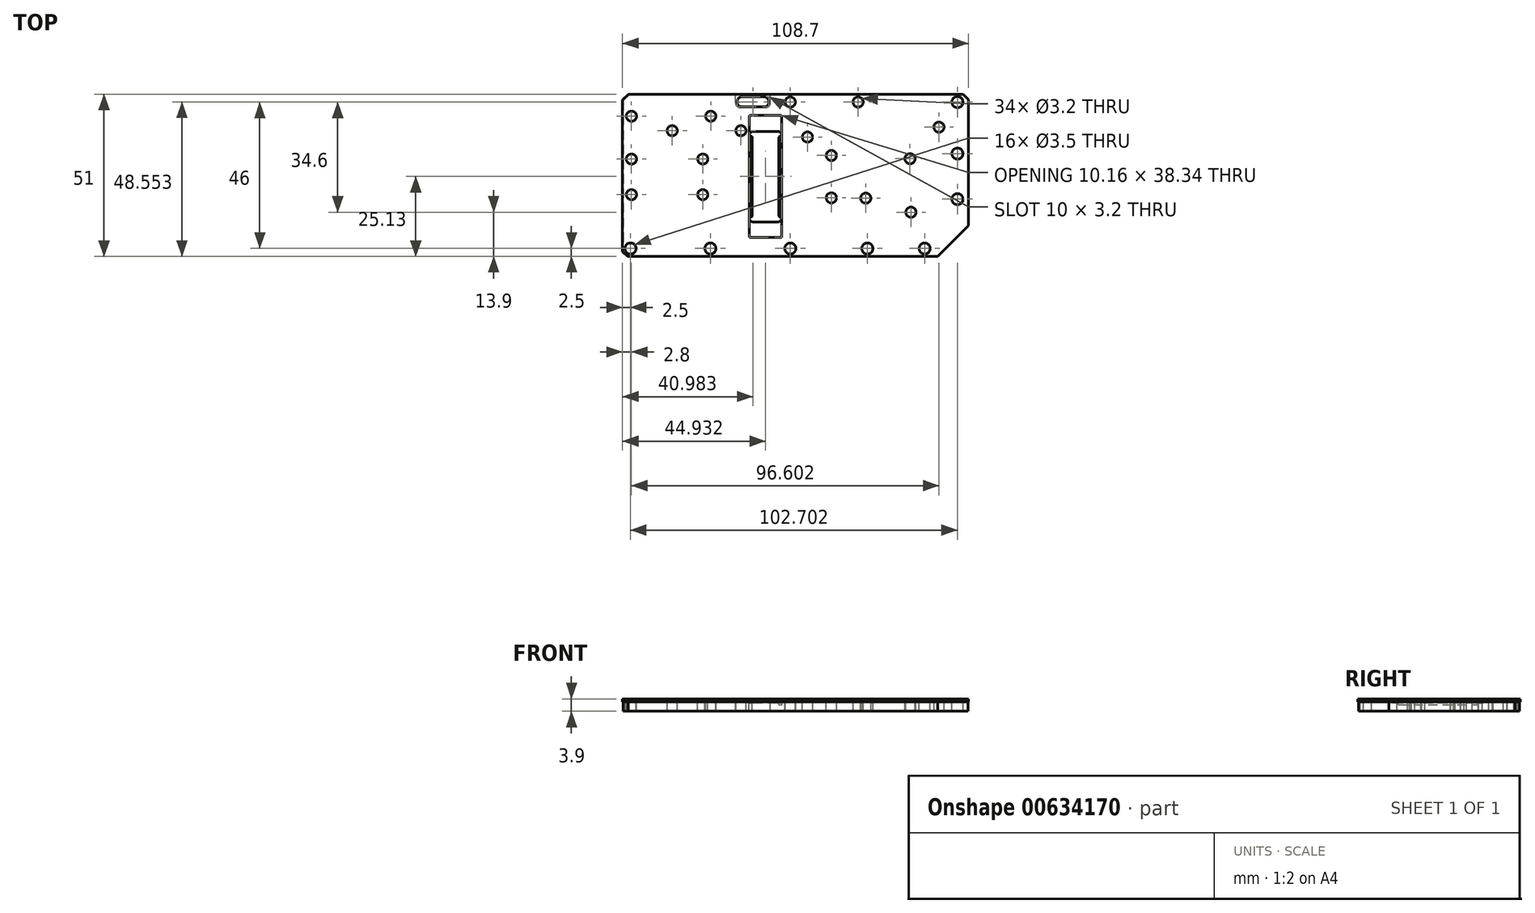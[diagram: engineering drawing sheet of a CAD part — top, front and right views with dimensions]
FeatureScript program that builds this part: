
annotation { "Feature Type Name" : "Feature", "Feature Type Description" : "" }
export const myFeature = defineFeature(function(context is Context, id is Id, definition is map)
    precondition{}
    {
        {
            var Q0;
            Q0=qCreatedBy(makeId("Top.planeOp"),FACE);
            var sketch = newSketch(context, id + "F0", { "sketchPlane" : qUnion([Q0])});
            skLineSegment(sketch, "E0", {"start": v(-19.36, 21.04) * mm, "end": v(-52.71, 21.04) * mm});
            skLineSegment(sketch, "E1", {"start": v(-52.71, 21.04) * mm, "end": v(-52.71, 24.84) * mm});
            skLineSegment(sketch, "E2", {"start": v(-52.71, 24.84) * mm, "end": v(-19.36, 24.84) * mm});
            skLineSegment(sketch, "E3", {"start": v(-19.36, 24.84) * mm, "end": v(-19.36, 21.04) * mm});
            skCircle(sketch, "E4", {"center": v(19.65, 23) * mm, "radius": 1.6 * mm});
            skCircle(sketch, "E5", {"center": v(-17.15, 14) * mm, "radius": 1.6 * mm});
            skCircle(sketch, "E6", {"center": v(-38.75, 14) * mm, "radius": 1.6 * mm});
            skCircle(sketch, "E7", {"center": v(36.25, -11.6) * mm, "radius": 1.6 * mm});
            skCircle(sketch, "E8", {"center": v(45.05, 15.1) * mm, "radius": 1.6 * mm});
            skCircle(sketch, "E9", {"center": v(3.75, 12) * mm, "radius": 1.6 * mm});
            skCircle(sketch, "E10", {"center": v(11.25, 6.2) * mm, "radius": 1.6 * mm});
            skCircle(sketch, "E11", {"center": v(22.05, -7.2) * mm, "radius": 1.6 * mm});
            skCircle(sketch, "E12", {"center": v(11.25, -7.1) * mm, "radius": 1.6 * mm});
            skCircle(sketch, "E13", {"center": v(-29.15, -6.1) * mm, "radius": 1.6 * mm});
            skCircle(sketch, "E14", {"center": v(-29.15, 5.1) * mm, "radius": 1.6 * mm});
            skCircle(sketch, "E15", {"center": v(-51.55, 5.1) * mm, "radius": 1.6 * mm});
            skCircle(sketch, "E16", {"center": v(-51.55, -6.1) * mm, "radius": 1.6 * mm});
            skCircle(sketch, "E17", {"center": v(-51.85, -23) * mm, "radius": 1.75 * mm});
            skCircle(sketch, "E18", {"center": v(-26.75, -23) * mm, "radius": 1.75 * mm});
            skCircle(sketch, "E19", {"center": v(-1.65, -23) * mm, "radius": 1.75 * mm});
            skCircle(sketch, "E20", {"center": v(22.55, -23) * mm, "radius": 1.75 * mm});
            skCircle(sketch, "E21", {"center": v(40.55, -23) * mm, "radius": 1.75 * mm});
            skCircle(sketch, "E22", {"center": v(50.85, -7.5) * mm, "radius": 1.75 * mm});
            skCircle(sketch, "E23", {"center": v(50.85, 6.8) * mm, "radius": 1.75 * mm});
            skCircle(sketch, "E24", {"center": v(50.85, 23) * mm, "radius": 1.75 * mm});
            skCircle(sketch, "E25", {"center": v(-1.65, 23) * mm, "radius": 1.6 * mm});
            skLineSegment(sketch, "E26", {"start": v(-54.35, -23.95) * mm, "end": v(-54.35, 23.6) * mm});
            skLineSegment(sketch, "E27", {"start": v(-54.35, 23.6) * mm, "end": v(-52.45, 25.5) * mm});
            skLineSegment(sketch, "E28", {"start": v(-52.45, 25.5) * mm, "end": v(52.7, 25.5) * mm});
            skLineSegment(sketch, "E29", {"start": v(52.7, 25.5) * mm, "end": v(54.35, 23.85) * mm});
            skLineSegment(sketch, "E30", {"start": v(54.35, 23.85) * mm, "end": v(54.35, -15.8) * mm});
            skLineSegment(sketch, "E31", {"start": v(54.35, -15.8) * mm, "end": v(44.65, -25.5) * mm});
            skLineSegment(sketch, "E32", {"start": v(44.65, -25.5) * mm, "end": v(-52.8, -25.5) * mm});
            skLineSegment(sketch, "E33", {"start": v(-52.8, -25.5) * mm, "end": v(-54.35, -23.95) * mm});
            skLineSegment(sketch, "E34", {"start": v(-4.34, -10.82) * mm, "end": v(-4.34, 9.88) * mm});
            skLineSegment(sketch, "E35", {"start": v(-14.5, 18.54) * mm, "end": v(-14.5, -19.28) * mm});
            skLineSegment(sketch, "E36", {"start": v(-4.34, -19.28) * mm, "end": v(-4.34, 18.54) * mm});
            skArc(sketch, "E37", {"start": v(-4.34, 18.54) * mm, "mid": v(-4.41, 18.72) * mm, "end": v(-4.6, 18.8) * mm});
            skLineSegment(sketch, "E38", {"start": v(-4.6, 18.8) * mm, "end": v(-14.24, 18.8) * mm});
            skArc(sketch, "E39", {"start": v(-14.24, 18.8) * mm, "mid": v(-14.42, 18.72) * mm, "end": v(-14.5, 18.54) * mm});
            skLineSegment(sketch, "E40", {"start": v(-14.24, -19.54) * mm, "end": v(-4.6, -19.54) * mm});
            skArc(sketch, "E41", {"start": v(-14.5, -19.28) * mm, "mid": v(-14.42, -19.46) * mm, "end": v(-14.24, -19.54) * mm});
            skArc(sketch, "E42", {"start": v(-4.6, -19.54) * mm, "mid": v(-4.41, -19.46) * mm, "end": v(-4.34, -19.28) * mm});
            skLineSegment(sketch, "E43", {"start": v(-54.35, 2.45) * mm, "end": v(-54.35, -3.2) * mm});
            skArc(sketch, "E44", {"start": v(-18.37, 23.05) * mm, "mid": v(-17.9, 24.18) * mm, "end": v(-16.77, 24.65) * mm});
            skLineSegment(sketch, "E45", {"start": v(-16.77, 24.65) * mm, "end": v(-9.97, 24.65) * mm});
            skArc(sketch, "E46", {"start": v(-9.97, 24.65) * mm, "mid": v(-8.84, 24.18) * mm, "end": v(-8.37, 23.05) * mm});
            skArc(sketch, "E47", {"start": v(-8.37, 23.05) * mm, "mid": v(-8.84, 21.92) * mm, "end": v(-9.97, 21.45) * mm});
            skLineSegment(sketch, "E48", {"start": v(-9.97, 21.45) * mm, "end": v(-16.77, 21.45) * mm});
            skArc(sketch, "E49", {"start": v(-16.77, 21.45) * mm, "mid": v(-17.9, 21.92) * mm, "end": v(-18.37, 23.05) * mm});
            skCircle(sketch, "E50", {"center": v(-51.55, 18.55) * mm, "radius": 1.6 * mm});
            skCircle(sketch, "E51", {"center": v(-26.65, 18.55) * mm, "radius": 1.6 * mm});
            skCircle(sketch, "E52", {"center": v(35.95, 5.2) * mm, "radius": 1.6 * mm});
            skSolve(sketch);
        }
        {
            var Q0;
            Q0=makeQuery(id+"F0.imprint","IMPRINT",FACE,{"disambiguationData":[TD([[makeQuery(id+"F0.imprint","IMPRINT",EDGE,{"derivedFrom":sQuery(id+"F0.wireOp",EDGE,"E0")}),1.0]])]});
            var Q1;
            Q1=makeQuery(id+"F0.imprint","IMPRINT",FACE,{"disambiguationData":[TD([[makeQuery(id+"F0.imprint","IMPRINT",EDGE,{"derivedFrom":sQuery(id+"F0.wireOp",EDGE,"E0")}),-1.0]])]});
            extrude(context, id + "F1", {"entities" : qUnion([Q0, Q1]), "depth" : 0.9 * mm, "offsetDistance" : 25 * mm});
        }
        {
            var Q0;
            Q0=qCreatedBy(makeId("Top.planeOp"),FACE);
            var sketch = newSketch(context, id + "F2", { "sketchPlane" : qUnion([Q0])});
            skLineSegment(sketch, "E53", {"start": v(-14.63, 12.3) * mm, "end": v(-14.63, -13.2) * mm});
            skArc(sketch, "E54", {"start": v(-14.63, -13.2) * mm, "mid": v(-14.19, -14.26) * mm, "end": v(-13.13, -14.7) * mm});
            skLineSegment(sketch, "E55", {"start": v(-13.13, -14.7) * mm, "end": v(-5.73, -14.7) * mm});
            skArc(sketch, "E56", {"start": v(-5.73, -14.7) * mm, "mid": v(-4.67, -14.26) * mm, "end": v(-4.23, -13.2) * mm});
            skLineSegment(sketch, "E57", {"start": v(-4.23, -13.2) * mm, "end": v(-4.23, 12.3) * mm});
            skArc(sketch, "E58", {"start": v(-4.23, 12.3) * mm, "mid": v(-4.67, 13.37) * mm, "end": v(-5.73, 13.8) * mm});
            skLineSegment(sketch, "E59", {"start": v(-5.73, 13.8) * mm, "end": v(-13.13, 13.8) * mm});
            skArc(sketch, "E60", {"start": v(-13.13, 13.8) * mm, "mid": v(-14.19, 13.37) * mm, "end": v(-14.63, 12.3) * mm});
            skLineSegment(sketch, "E61", {"start": v(-18.87, 22.75) * mm, "end": v(-18.87, 25.3) * mm});
            skLineSegment(sketch, "E62", {"start": v(-7.87, 22.75) * mm, "end": v(-7.87, 25.3) * mm});
            skLineSegment(sketch, "E63", {"start": v(-9.37, 21.25) * mm, "end": v(-17.37, 21.25) * mm});
            skArc(sketch, "E64", {"start": v(-18.87, 22.75) * mm, "mid": v(-18.43, 21.7) * mm, "end": v(-17.37, 21.25) * mm});
            skArc(sketch, "E65", {"start": v(-9.37, 21.25) * mm, "mid": v(-8.3, 21.7) * mm, "end": v(-7.87, 22.75) * mm});
            skLineSegment(sketch, "E66", {"start": v(-54.15, 23.4) * mm, "end": v(-54.15, -23.8) * mm});
            skLineSegment(sketch, "E67", {"start": v(-54.15, -23.8) * mm, "end": v(-52.65, -25.3) * mm});
            skLineSegment(sketch, "E68", {"start": v(-52.65, -25.3) * mm, "end": v(44.65, -25.3) * mm});
            skLineSegment(sketch, "E69", {"start": v(44.65, -25.3) * mm, "end": v(54.15, -15.8) * mm});
            skLineSegment(sketch, "E70", {"start": v(54.15, -15.8) * mm, "end": v(54.15, 23.8) * mm});
            skLineSegment(sketch, "E71", {"start": v(54.15, 23.8) * mm, "end": v(52.65, 25.3) * mm});
            skLineSegment(sketch, "E72", {"start": v(-18.87, 25.3) * mm, "end": v(-52.25, 25.3) * mm});
            skLineSegment(sketch, "E73", {"start": v(-52.25, 25.3) * mm, "end": v(-54.15, 23.4) * mm});
            skLineSegment(sketch, "E74", {"start": v(-7.87, 25.3) * mm, "end": v(52.65, 25.3) * mm});
            skLineSegment(sketch, "E75", {"start": v(-14.63, -12.7) * mm, "end": v(-14.63, 11.8) * mm});
            skArc(sketch, "E76", {"start": v(-14.63, 11.8) * mm, "mid": v(-14.48, 12.16) * mm, "end": v(-14.13, 12.3) * mm});
            skArc(sketch, "E77", {"start": v(-14.13, 12.3) * mm, "mid": v(-13.77, 12.16) * mm, "end": v(-13.63, 11.8) * mm});
            skLineSegment(sketch, "E78", {"start": v(-13.63, 11.8) * mm, "end": v(-13.63, -12.7) * mm});
            skArc(sketch, "E79", {"start": v(-13.63, -12.7) * mm, "mid": v(-13.77, -13.05) * mm, "end": v(-14.13, -13.2) * mm});
            skArc(sketch, "E80", {"start": v(-14.13, -13.2) * mm, "mid": v(-14.48, -13.05) * mm, "end": v(-14.63, -12.7) * mm});
            skLineSegment(sketch, "E81", {"start": v(-5.23, -12.7) * mm, "end": v(-5.23, 11.8) * mm});
            skArc(sketch, "E82", {"start": v(-5.23, 11.8) * mm, "mid": v(-5.08, 12.16) * mm, "end": v(-4.73, 12.3) * mm});
            skArc(sketch, "E83", {"start": v(-4.73, 12.3) * mm, "mid": v(-4.37, 12.16) * mm, "end": v(-4.23, 11.8) * mm});
            skLineSegment(sketch, "E84", {"start": v(-4.23, 11.8) * mm, "end": v(-4.23, -12.7) * mm});
            skArc(sketch, "E85", {"start": v(-4.23, -12.7) * mm, "mid": v(-4.37, -13.05) * mm, "end": v(-4.73, -13.2) * mm});
            skArc(sketch, "E86", {"start": v(-4.73, -13.2) * mm, "mid": v(-5.08, -13.05) * mm, "end": v(-5.23, -12.7) * mm});
            skCircle(sketch, "E87", {"center": v(-51.55, 18.55) * mm, "radius": 1.6 * mm});
            skCircle(sketch, "E88", {"center": v(-38.75, 14) * mm, "radius": 1.6 * mm});
            skCircle(sketch, "E89", {"center": v(-26.65, 18.55) * mm, "radius": 1.6 * mm});
            skCircle(sketch, "E90", {"center": v(-1.65, 23) * mm, "radius": 1.6 * mm});
            skCircle(sketch, "E91", {"center": v(-17.15, 14) * mm, "radius": 1.6 * mm});
            skCircle(sketch, "E92", {"center": v(-29.15, 5.1) * mm, "radius": 1.6 * mm});
            skCircle(sketch, "E93", {"center": v(-51.55, 5.1) * mm, "radius": 1.6 * mm});
            skCircle(sketch, "E94", {"center": v(-51.55, -6.1) * mm, "radius": 1.6 * mm});
            skCircle(sketch, "E95", {"center": v(-29.15, -6.1) * mm, "radius": 1.6 * mm});
            skCircle(sketch, "E96", {"center": v(19.65, 23) * mm, "radius": 1.6 * mm});
            skCircle(sketch, "E97", {"center": v(50.85, 23) * mm, "radius": 1.75 * mm});
            skCircle(sketch, "E98", {"center": v(50.85, 6.8) * mm, "radius": 1.75 * mm});
            skCircle(sketch, "E99", {"center": v(11.25, 6.2) * mm, "radius": 1.6 * mm});
            skCircle(sketch, "E100", {"center": v(3.75, 12) * mm, "radius": 1.6 * mm});
            skCircle(sketch, "E101", {"center": v(11.25, -7.1) * mm, "radius": 1.6 * mm});
            skCircle(sketch, "E102", {"center": v(22.05, -7.2) * mm, "radius": 1.6 * mm});
            skCircle(sketch, "E103", {"center": v(36.25, -11.6) * mm, "radius": 1.6 * mm});
            skCircle(sketch, "E104", {"center": v(50.85, -7.5) * mm, "radius": 1.75 * mm});
            skCircle(sketch, "E105", {"center": v(40.55, -23) * mm, "radius": 1.75 * mm});
            skCircle(sketch, "E106", {"center": v(22.55, -23) * mm, "radius": 1.75 * mm});
            skCircle(sketch, "E107", {"center": v(-1.65, -23) * mm, "radius": 1.75 * mm});
            skCircle(sketch, "E108", {"center": v(-26.75, -23) * mm, "radius": 1.75 * mm});
            skCircle(sketch, "E109", {"center": v(-51.85, -23) * mm, "radius": 1.75 * mm});
            skCircle(sketch, "E110", {"center": v(45.05, 15.1) * mm, "radius": 1.6 * mm});
            skCircle(sketch, "E111", {"center": v(35.95, 5.2) * mm, "radius": 1.6 * mm});
            skSolve(sketch);
        }
        {
            var Q0;
            {var subQ7=sQuery(id+"F2.wireOp",EDGE,"E54");Q0=makeQuery(id+"F2.imprint","IMPRINT",FACE,{"disambiguationData":[TD([[makeQuery(id+"F2.imprint","IMPRINT",EDGE,{"derivedFrom":subQ7}),-1.0]])]});}
            var Q1;
            {var subQ11=sQuery(id+"F2.wireOp",EDGE,"E54");Q1=makeQuery(id+"F2.imprint","IMPRINT",FACE,{"disambiguationData":[TD([[makeQuery(id+"F2.imprint","IMPRINT",EDGE,{"derivedFrom":subQ11}),1.0]])]});}
            var Q2;
            Q2=makeQuery(id+"F2.imprint","IMPRINT",FACE,{"disambiguationData":[TD([[makeQuery(id+"F2.imprint","IMPRINT",EDGE,{"derivedFrom":sQuery(id+"F2.wireOp",EDGE,"E75")}),-1.0]])]});
            var Q3;
            Q3=makeQuery(id+"F2.imprint","IMPRINT",FACE,{"disambiguationData":[TD([[makeQuery(id+"F2.imprint","IMPRINT",EDGE,{"derivedFrom":sQuery(id+"F2.wireOp",EDGE,"E81")}),-1.0]])]});
            extrude(context, id + "F3", {"entities" : qUnion([Q0, Q1, Q2, Q3]), "oppositeDirection" : true, "depth" : 3 * mm, "offsetDistance" : 25 * mm});
        }
        {
            var Q0;
            {var subQ11=sQuery(id+"F2.wireOp",EDGE,"E54");Q0=makeQuery(id+"F2.imprint","IMPRINT",FACE,{"disambiguationData":[TD([[makeQuery(id+"F2.imprint","IMPRINT",EDGE,{"derivedFrom":subQ11}),1.0]])]});}
            extrude(context, id + "F4", {"entities" : qUnion([Q0]), "operationType" : NewBodyOperationType.REMOVE, "oppositeDirection" : true, "depth" : 0.45 * mm, "offsetDistance" : 25 * mm});
        }
        {
            var Q0;
            Q0=makeQuery(id+"F2.imprint","IMPRINT",FACE,{"disambiguationData":[TD([[makeQuery(id+"F2.imprint","IMPRINT",EDGE,{"derivedFrom":sQuery(id+"F2.wireOp",EDGE,"E75")}),-1.0]])]});
            var Q1;
            Q1=makeQuery(id+"F2.imprint","IMPRINT",FACE,{"disambiguationData":[TD([[makeQuery(id+"F2.imprint","IMPRINT",EDGE,{"derivedFrom":sQuery(id+"F2.wireOp",EDGE,"E81")}),-1.0]])]});
            extrude(context, id + "F5", {"entities" : qUnion([Q0, Q1]), "operationType" : NewBodyOperationType.REMOVE, "oppositeDirection" : true, "depth" : 0.9 * mm, "offsetDistance" : 25 * mm});
        }
    });
